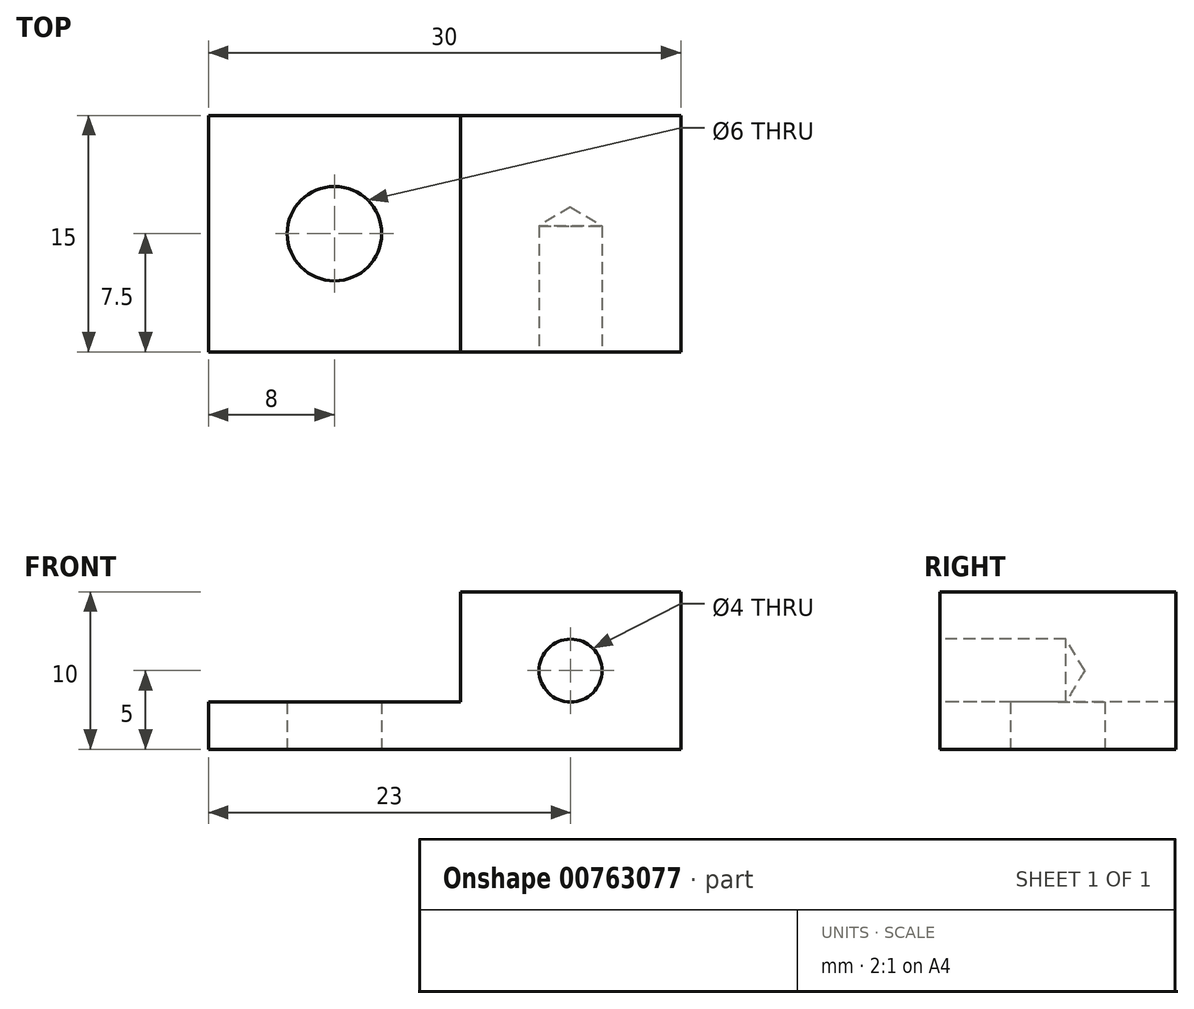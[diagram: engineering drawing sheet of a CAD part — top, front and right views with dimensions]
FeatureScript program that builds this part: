
annotation { "Feature Type Name" : "Feature", "Feature Type Description" : "" }
export const myFeature = defineFeature(function(context is Context, id is Id, definition is map)
    precondition{}
    {
        {
            var Q0;
            Q0=qCreatedBy(makeId("Top.planeOp"),FACE);
            var sketch = newSketch(context, id + "F0", { "sketchPlane" : qUnion([Q0])});
            skLineSegment(sketch, "E0.bottom", {"start": v(15, -7.5) * mm, "end": v(-15, -7.5) * mm});
            skLineSegment(sketch, "E0.top", {"start": v(15, 7.5) * mm, "end": v(-15, 7.5) * mm});
            skLineSegment(sketch, "E0.left", {"start": v(15, -7.5) * mm, "end": v(15, 7.5) * mm});
            skLineSegment(sketch, "E0.right", {"start": v(-15, -7.5) * mm, "end": v(-15, 7.5) * mm});
            skPoint(sketch, "E0.middle", {"position": v(0, 0) * mm});
            skPoint(sketch, "E1", {"position": v(-7, 0) * mm});
            skSolve(sketch);
        }
        {
            var Q0;
            Q0 = qSketchRegion(id + "F0", true);
            extrude(context, id + "F1", {"entities" : qUnion([Q0]), "depth" : 10 * mm, "offsetDistance" : 25 * mm});
        }
        {
            var Q0;
            Q0=sQuery(id+"F0.wireOp",VERTEX,"E1");
            var Q1;
            Q1=makeQuery(id+"F1.opExtrude","SWEPT_BODY",BODY,{"disambiguationData":[OSD([sQuery(id+"F0.wireOp",EDGE,"E0.bottom"),sQuery(id+"F0.wireOp",EDGE,"E0.top"),sQuery(id+"F0.wireOp",EDGE,"E0.left"),sQuery(id+"F0.wireOp",EDGE,"E0.right")])]});
            hole(context, id + "F2", {"style" : HoleStyle.SIMPLE, "endStyle" : HoleEndStyle.THROUGH, "oppositeDirection" : true, "holeDiameter" : 6 * mm, "majorDiameter" : 5 * mm, "isTappedThrough" : true, "tappedDepth" : 12 * mm, "tapClearance" : 3, "locations" : qUnion([Q0]), "scope" : qUnion([Q1])});
        }
        {
            var Q0;
            Q0=makeQuery(id+"F1.opExtrude","SWEPT_FACE",FACE,{"disambiguationData":[OSD([sQuery(id+"F0.wireOp",EDGE,"E0.bottom")])]});
            var sketch = newSketch(context, id + "F3", { "sketchPlane" : qUnion([Q0])});
            skPoint(sketch, "E2", {"position": v(8, 5) * mm});
            skSolve(sketch);
        }
        {
            var Q0;
            Q0=sQuery(id+"F3.wireOp",VERTEX,"E2");
            var Q1;
            Q1=makeQuery(id+"F1.opExtrude","SWEPT_BODY",BODY,{"disambiguationData":[OSD([sQuery(id+"F0.wireOp",EDGE,"E0.bottom"),sQuery(id+"F0.wireOp",EDGE,"E0.top"),sQuery(id+"F0.wireOp",EDGE,"E0.left"),sQuery(id+"F0.wireOp",EDGE,"E0.right")])]});
            hole(context, id + "F4", {"style" : HoleStyle.SIMPLE, "endStyle" : HoleEndStyle.BLIND, "holeDiameter" : 4 * mm, "majorDiameter" : 5 * mm, "holeDepth" : 8 * mm, "isTappedThrough" : true, "tappedDepth" : 12 * mm, "tapClearance" : 3, "locations" : qUnion([Q0]), "scope" : qUnion([Q1])});
        }
        {
            var Q0;
            Q0=qCreatedBy(makeId("Front.planeOp"),FACE);
            var sketch = newSketch(context, id + "F5", { "sketchPlane" : qUnion([Q0])});
            skLineSegment(sketch, "E3.bottom", {"start": v(1, 3) * mm, "end": v(-15, 3) * mm});
            skLineSegment(sketch, "E3.top", {"start": v(1, 10) * mm, "end": v(-15, 10) * mm});
            skLineSegment(sketch, "E3.left", {"start": v(1, 3) * mm, "end": v(1, 10) * mm});
            skLineSegment(sketch, "E3.right", {"start": v(-15, 3) * mm, "end": v(-15, 10) * mm});
            skPoint(sketch, "E3.middle", {"position": v(-7, 6.5) * mm});
            skSolve(sketch);
        }
        {
            var Q0;
            Q0 = qSketchRegion(id + "F5", true);
            extrude(context, id + "F6", {"entities" : qUnion([Q0]), "operationType" : NewBodyOperationType.REMOVE, "endBound" : BoundingType.SYMMETRIC, "oppositeDirection" : true, "depth" : 15 * mm, "offsetDistance" : 25 * mm});
        }
    });
